# Revit family: Honeywell_PowerSupply_HLS-PS
name_source: partatom
category: Electrical Equipment
revit_build: Autodesk Revit 2017 (Build: 20160225_1515(x64)
units: mm (PartAtom-declared; Revit-internal decimal feet)

## family parameters
Always vertical = Yes
Cut with Voids When Loaded = No
OmniClass Number = 23.80.30.11.17
OmniClass Title = Distribution Boards and Control Panels
Part Type = Transformer
Room Calculation Point = No
Round Connector Dimension = Use Radius
Shared = No
Work Plane-Based = No

## types (2) — shared parameters
Assembly Code = D5090200
BatteriesChargeCurrentMax = 1 A
BatteriesChargeCurrentMin = 0 A
BatteriesSpace = 2x17AH
Depth = 97 mm  [stored 0.318241 ft]
Description = Power supply designed in order to support fire control systems
FaultRelay = C, NA, NC contacts 1A/24V maximum. Energized in normal status.
FrequencyMax = 60 Hz
FrequencyMin = 50 Hz
Ground Bus = No
GroundConnectorSurveillance = Desactivable
Height = 410 mm  [stored 1.34514 ft]
LoadClassification = Power
Manufacturer = Honeywell Life Safety Iberia
Material = Steel, Black
OutputTension = 28 V
SecurityStandards = Designed following EN54-4, EN55022:211 +AC:2012
Designed following EN54-4, EN55022:211 +AC:2012
SingleOutputConversion = Yes, with SW1 microswitch
StatusLEDExteriorNumber = 10
StatusLEDInteriorNumber = 7
SubFeed Lugs = No
SupplyOutputsNumber = 2
Type Comments = * Delete unused conduit connectors for a better performance
URL = https://www.honeywelllifesafety.es
VibrationsTest = 10-500 Hz 2G 10'/1 cicle during 60' per axis
Voltage = 28
Width = 380 mm  [stored 1.24672 ft]

## per-type parameters (varying)
| type | ApparentPower | CurrentPerOutputMax | CurrentUsingSingleOutputMax | Model | Wattage |
| HLS-PS25 | 65 W | 1 A | 2 A | HLS-PS-25 | 65 |
| HLS-PS50 | 130 W | 2 A | 4 A | HLS-PS-50 | 130 |

note: [stored X ft] marks values corroborated as IEEE doubles in the binary element streams (Revit-internal decimal feet)

## geometry (parser evidence)
native form markers: Sweep x3
no freeform markers — native parametric forms only
